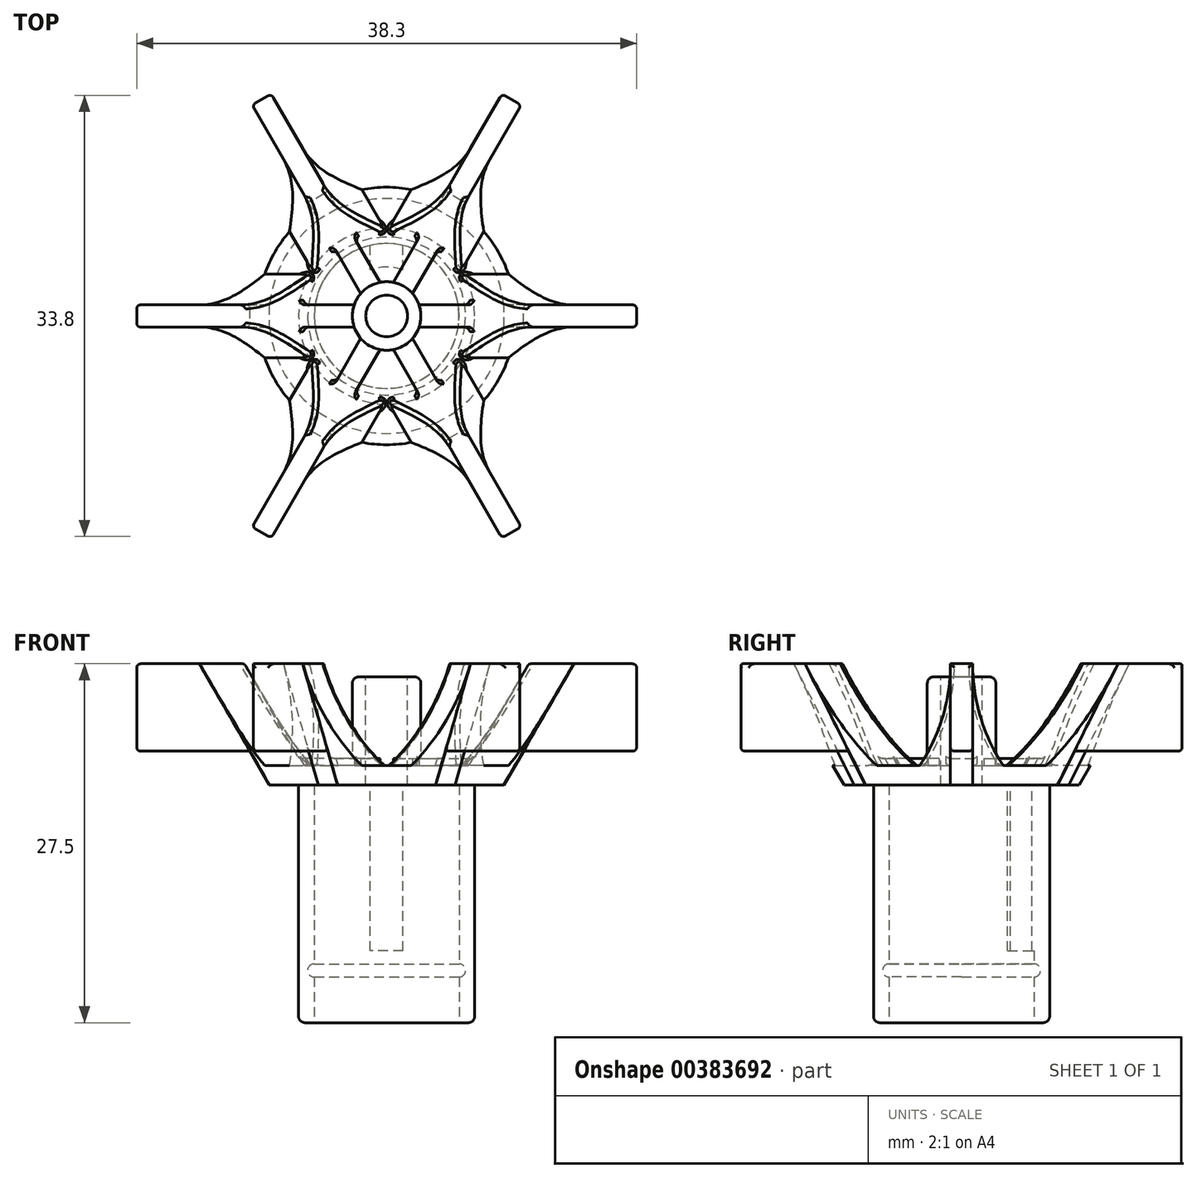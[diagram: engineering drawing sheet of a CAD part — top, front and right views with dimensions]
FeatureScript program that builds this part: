
annotation { "Feature Type Name" : "Feature", "Feature Type Description" : "" }
export const myFeature = defineFeature(function(context is Context, id is Id, definition is map)
    precondition{}
    {
        {
            var Q0;
            Q0=qCreatedBy(makeId("Top.planeOp"),FACE);
            cPlane(context, id + "F0", {"entities" : qUnion([Q0]), "cplaneType" : CPlaneType.OFFSET, "offset" : 26.5 * mm, "width" : 152.4 * mm, "height" : 152.4 * mm});
        }
        {
            var Q0;
            Q0=qCreatedBy(makeId("Front.planeOp"),FACE);
            var sketch = newSketch(context, id + "F1", { "sketchPlane" : qUnion([Q0])});
            skLineSegment(sketch, "E0", {"start": v(0, 29.25) * mm, "end": v(0, 3.34) * mm, "construction": true});
            skSolve(sketch);
        }
        {
            var Q0;
            Q0=qCreatedBy(makeId("Top.planeOp"),FACE);
            var sketch = newSketch(context, id + "F2", { "sketchPlane" : qUnion([Q0])});
            skCircle(sketch, "E1", {"center": v(0, 0) * mm, "radius": 6.75 * mm});
            skSolve(sketch);
        }
        {
            var Q0;
            Q0=makeQuery(id+"F2.imprint","IMPRINT",FACE,{"disambiguationData":[TD([[makeQuery(id+"F2.imprint","IMPRINT",EDGE,{"derivedFrom":sQuery(id+"F2.wireOp",EDGE,"E1")}),1.0]])]});
            extrude(context, id + "F3", {"entities" : qUnion([Q0]), "depth" : 19.7 * mm});
        }
        {
            var Q0;
            Q0=makeQuery(id+"F3.opExtrude","CAP_FACE",FACE,{"disambiguationData":[OSD([sQuery(id+"F2.wireOp",EDGE,"E1")])],"isStart":false});
            var sketch = newSketch(context, id + "F4", { "sketchPlane" : qUnion([Q0])});
            skCircle(sketch, "E2", {"center": v(0, 0) * mm, "radius": 8.38 * mm});
            skSolve(sketch);
        }
        {
            var Q0;
            Q0 = qSketchRegion(id + "F4", true);
            extrude(context, id + "F5", {"entities" : qUnion([Q0]), "operationType" : NewBodyOperationType.ADD, "oppositeDirection" : true, "depth" : 1.5 * mm});
        }
        {
            var Q0;
            Q0=makeQuery(id+"F3.opExtrude","CAP_FACE",FACE,{"disambiguationData":[OSD([sQuery(id+"F2.wireOp",EDGE,"E1")])],"isStart":true});
            var sketch = newSketch(context, id + "F6", { "sketchPlane" : qUnion([Q0])});
            skCircle(sketch, "E3", {"center": v(0, 0) * mm, "radius": 5.55 * mm});
            skSolve(sketch);
        }
        {
            var Q0;
            Q0=makeQuery(id+"F6.imprint","IMPRINT",FACE,{"disambiguationData":[TD([[makeQuery(id+"F6.imprint","IMPRINT",EDGE,{"derivedFrom":sQuery(id+"F6.wireOp",EDGE,"E3")}),1.0]])]});
            var Q1;
            Q1=makeQuery(id+"F5.opExtrude","CAP_FACE",FACE,{"disambiguationData":[OSD([sQuery(id+"F4.wireOp",EDGE,"E2")])],"isStart":false});
            extrude(context, id + "F7", {"entities" : qUnion([Q0]), "operationType" : NewBodyOperationType.REMOVE, "endBound" : BoundingType.UP_TO_SURFACE, "oppositeDirection" : true, "endBoundEntityFace" : qUnion([Q1]), "depth" : 25.4 * mm});
        }
        {
            var Q0;
            Q0=makeQuery(id+"F5.boolean.opBoolean","MERGE",FACE,{"derivedFrom":[makeQuery(id+"F3.opExtrude","CAP_FACE",FACE,{"disambiguationData":[OSD([sQuery(id+"F2.wireOp",EDGE,"E1")])],"isStart":false}),makeQuery(id+"F5.opExtrude","CAP_FACE",FACE,{"disambiguationData":[OSD([sQuery(id+"F4.wireOp",EDGE,"E2")])],"isStart":true})]});
            var sketch = newSketch(context, id + "F8", { "sketchPlane" : qUnion([Q0])});
            skCircle(sketch, "E4", {"center": v(0, 0) * mm, "radius": 2.62 * mm});
            skSolve(sketch);
        }
        {
            var Q0;
            Q0 = qSketchRegion(id + "F8", true);
            var Q1;
            Q1=qCreatedBy(id+"F0.planeOp",FACE);
            extrude(context, id + "F9", {"entities" : qUnion([Q0]), "operationType" : NewBodyOperationType.ADD, "endBound" : BoundingType.UP_TO_SURFACE, "endBoundEntityFace" : qUnion([Q1]), "depth" : 25.4 * mm});
        }
        {
            var Q0;
            Q0=makeQuery(id+"F9.opExtrude","CAP_FACE",FACE,{"disambiguationData":[OSD([sQuery(id+"F8.wireOp",EDGE,"E4")])],"isStart":false});
            var sketch = newSketch(context, id + "F10", { "sketchPlane" : qUnion([Q0])});
            skCircle(sketch, "E5", {"center": v(0, 0) * mm, "radius": 1.6 * mm});
            skSolve(sketch);
        }
        {
            var Q0;
            Q0 = qSketchRegion(id + "F10", true);
            extrude(context, id + "F11", {"entities" : qUnion([Q0]), "operationType" : NewBodyOperationType.REMOVE, "endBound" : BoundingType.THROUGH_ALL, "oppositeDirection" : true, "depth" : 25.4 * mm});
        }
        {
            var Q0;
            Q0=qCreatedBy(makeId("Front.planeOp"),FACE);
            var sketch = newSketch(context, id + "F12", { "sketchPlane" : qUnion([Q0])});
            skLineSegment(sketch, "E6", {"start": v(1.6, 19.7) * mm, "end": v(1.6, 20.25) * mm});
            skLineSegment(sketch, "E7", {"start": v(1.6, 20.25) * mm, "end": v(6.72, 20.25) * mm});
            skLineSegment(sketch, "E8", {"start": v(6.72, 20.25) * mm, "end": v(10.9, 27.5) * mm});
            skLineSegment(sketch, "E9", {"start": v(10.9, 27.5) * mm, "end": v(19.15, 27.5) * mm});
            skLineSegment(sketch, "E10", {"start": v(19.15, 27.5) * mm, "end": v(19.15, 20.8) * mm});
            skLineSegment(sketch, "E11", {"start": v(19.15, 20.8) * mm, "end": v(10.5, 20.8) * mm});
            skLineSegment(sketch, "E12", {"start": v(10.5, 20.8) * mm, "end": v(9, 18.2) * mm});
            skLineSegment(sketch, "E13", {"start": v(9, 18.2) * mm, "end": v(6.75, 18.2) * mm});
            skLineSegment(sketch, "E14", {"start": v(6.75, 18.2) * mm, "end": v(6.75, 19.7) * mm});
            skLineSegment(sketch, "E15", {"start": v(6.75, 19.7) * mm, "end": v(1.6, 19.7) * mm});
            skLineSegment(sketch, "E16", {"start": v(1.6, 20.25) * mm, "end": v(1.6, 26.5) * mm, "construction": true});
            skSolve(sketch);
        }
        {
            var Q0;
            Q0 = qSketchRegion(id + "F12", true);
            extrude(context, id + "F13", {"entities" : qUnion([Q0]), "operationType" : NewBodyOperationType.ADD, "endBound" : BoundingType.SYMMETRIC, "depth" : 1.7 * mm});
        }
        {
            var Q0;
            Q0=makeQuery(id+"F9.opExtrude","CAP_EDGE",EDGE,{"disambiguationData":[OSD([sQuery(id+"F8.wireOp",EDGE,"E4")])],"isStart":false});
            var Q1;
            Q1=makeQuery(id+"FnX98SisdUr0QIh_1.opPattern","COPY",EDGE,{"derivedFrom":makeQuery(id+"F5.opExtrude","CAP_EDGE",EDGE,{"disambiguationData":[OSD([sQuery(id+"F4.wireOp",EDGE,"E2")])],"isStart":true}),"instanceName":"2"});
            var Q2;
            Q2=makeQuery(id+"F7.boolean.opBoolean","COPY",EDGE,{"derivedFrom":makeQuery(id+"F7.opExtrude","CAP_EDGE",EDGE,{"disambiguationData":[OSD([sQuery(id+"F6.wireOp",EDGE,"E3")])],"isStart":true})});
            var Q3;
            Q3=makeQuery(id+"F3.opExtrude","CAP_EDGE",EDGE,{"disambiguationData":[OSD([sQuery(id+"F2.wireOp",EDGE,"E1")])],"isStart":true});
            var Q4;
            Q4=makeQuery(id+"F5.opExtrude","CAP_EDGE",EDGE,{"disambiguationData":[OSD([sQuery(id+"F4.wireOp",EDGE,"E2")])],"isStart":true});
            var Q5;
            Q5=makeQuery(id+"F9.opExtrude","CAP_EDGE",EDGE,{"disambiguationData":[OSD([sQuery(id+"F8.wireOp",EDGE,"E4")])],"isStart":true});
            fillet(context, id + "F14", {"entities" : qUnion([Q0, Q1, Q2, Q3, Q4, Q5]), "radius" : .5 * mm, "tangentPropagation" : true, "allowEdgeOverflow" : false});
        }
        {
            var Q0;
            Q0=qCreatedBy(makeId("Front.planeOp"),FACE);
            var sketch = newSketch(context, id + "F15", { "sketchPlane" : qUnion([Q0])});
            skLineSegment(sketch, "E17", {"start": v(14.37, 27.5) * mm, "end": v(10.9, 27.5) * mm});
            skLineSegment(sketch, "E18", {"start": v(10.9, 27.5) * mm, "end": v(5.54, 18.2) * mm});
            skLineSegment(sketch, "E19", {"start": v(5.54, 18.2) * mm, "end": v(9, 18.2) * mm});
            skLineSegment(sketch, "E20", {"start": v(9, 18.2) * mm, "end": v(14.37, 27.5) * mm});
            skSolve(sketch);
        }
        {
            var Q0;
            Q0 = qSketchRegion(id + "F15", true);
            var Q1;
            Q1=sQuery(id+"F1.wireOp",EDGE,"E0");
            revolve(context, id + "F16", {"operationType" : NewBodyOperationType.ADD, "entities" : qUnion([Q0]), "axis" : qUnion([Q1]), "revolveType" : RevolveType.SYMMETRIC, "angle" : 60 * degree});
        }
        {
            var Q0;
            Q0=qCreatedBy(makeId("Right.planeOp"),FACE);
            cPlane(context, id + "F17", {"entities" : qUnion([Q0]), "cplaneType" : CPlaneType.OFFSET, "offset" : 4.65 * mm, "width" : 152.4 * mm, "height" : 152.4 * mm});
        }
        {
            var Q0;
            Q0=qCreatedBy(id+"F17.planeOp",FACE);
            var sketch = newSketch(context, id + "F18", { "sketchPlane" : qUnion([Q0])});
            skPoint(sketch, "E21", {"position": v(4.93, 19.7) * mm});
            skLineSegment(sketch, "E22", {"start": v(0.85, 27.5) * mm, "end": v(7.18, 27.5) * mm});
            skLineSegment(sketch, "E23", {"start": v(7.18, 27.5) * mm, "end": v(4.93, 19.7) * mm});
            skLineSegment(sketch, "E24.MirrorCS", {"start": v(-0.85, 27.5) * mm, "end": v(-7.18, 27.5) * mm});
            skLineSegment(sketch, "E25.MirrorCS", {"start": v(-7.18, 27.5) * mm, "end": v(-4.93, 19.7) * mm});
            skPoint(sketch, "E26.MirrorCS.end.orphan", {"position": v(-4.93, 19.7) * mm});
            skPoint(sketch, "E26.MirrorCS.start.orphan", {"position": v(-0.85, 27.5) * mm});
            skLineSegment(sketch, "E27", {"start": v(4.93, 19.7) * mm, "end": v(3.2, 19.7) * mm});
            skArc(sketch, "E28", {"start": v(0.85, 27.5) * mm, "mid": v(1.45, 23.43) * mm, "end": v(3.2, 19.7) * mm});
            skLineSegment(sketch, "E29", {"start": v(0.85, 27.5) * mm, "end": v(0.85, 19.7) * mm, "construction": true});
            skArc(sketch, "E30.MirrorCS", {"start": v(-0.85, 27.5) * mm, "mid": v(-1.45, 23.43) * mm, "end": v(-3.2, 19.7) * mm});
            skLineSegment(sketch, "E31.MirrorCS", {"start": v(-4.93, 19.7) * mm, "end": v(-3.2, 19.7) * mm});
            skSolve(sketch);
        }
        {
            var Q0;
            Q0 = qSketchRegion(id + "F18", true);
            var Q1;
            Q1=makeQuery(id+"F13.opExtrude","SWEPT_FACE",FACE,{"disambiguationData":[OSD([sQuery(id+"F12.wireOp",EDGE,"E10")])]});
            extrude(context, id + "F19", {"entities" : qUnion([Q0]), "operationType" : NewBodyOperationType.REMOVE, "endBound" : BoundingType.UP_TO_SURFACE, "endBoundEntityFace" : qUnion([Q1]), "depth" : 25.4 * mm});
        }
        {
            var Q0;
            Q0=makeQuery(id+"F19.boolean.opBoolean","INTERSECT",EDGE,{"derivedFrom":[makeQuery(id+"F16.opRevolve","SWEPT_FACE",FACE,{"disambiguationData":[OSD([sQuery(id+"F15.wireOp",EDGE,"E18")])]}),makeQuery(id+"F19.opExtrude","SWEPT_FACE",FACE,{"disambiguationData":[OSD([sQuery(id+"F18.wireOp",EDGE,"E28")])]})]});
            var Q1;
            Q1=makeQuery(id+"F16.opRevolve","SWEPT_EDGE",EDGE,{"disambiguationData":[OSD([sQuery(id+"F15.wireOp",EDGE,"E17"),sQuery(id+"F15.wireOp",EDGE,"E18")])]});
            var Q2;
            Q2=makeQuery(id+"F19.boolean.opBoolean","INTERSECT",EDGE,{"derivedFrom":[makeQuery(id+"F16.opRevolve","SWEPT_FACE",FACE,{"disambiguationData":[OSD([sQuery(id+"F15.wireOp",EDGE,"E18")])]}),makeQuery(id+"F19.opExtrude","SWEPT_FACE",FACE,{"disambiguationData":[OSD([sQuery(id+"F18.wireOp",EDGE,"E30.MirrorCS")])]})]});
            var Q3;
            Q3=makeQuery(id+"F16.boolean.opBoolean","INTERSECT",EDGE,{"disambiguationData":[OD(0.0)],"derivedFrom":[makeQuery(id+"F5.boolean.opBoolean","MERGE",FACE,{"derivedFrom":[makeQuery(id+"F3.opExtrude","CAP_FACE",FACE,{"disambiguationData":[OSD([sQuery(id+"F2.wireOp",EDGE,"E1")])],"isStart":false}),makeQuery(id+"F5.opExtrude","CAP_FACE",FACE,{"disambiguationData":[OSD([sQuery(id+"F4.wireOp",EDGE,"E2")])],"isStart":true})]}),makeQuery(id+"F16.opRevolve","SWEPT_FACE",FACE,{"disambiguationData":[OSD([sQuery(id+"F15.wireOp",EDGE,"E18")])]})]});
            var Q4;
            Q4=makeQuery(id+"F16.boolean.opBoolean","INTERSECT",EDGE,{"derivedFrom":[makeQuery(id+"F13.opExtrude","SWEPT_FACE",FACE,{"disambiguationData":[OSD([sQuery(id+"F12.wireOp",EDGE,"E7")])]}),makeQuery(id+"F16.opRevolve","SWEPT_FACE",FACE,{"disambiguationData":[OSD([sQuery(id+"F15.wireOp",EDGE,"E18")])]})]});
            var Q5;
            Q5=makeQuery(id+"F16.boolean.opBoolean","INTERSECT",EDGE,{"disambiguationData":[OD(1.0)],"derivedFrom":[makeQuery(id+"F5.boolean.opBoolean","MERGE",FACE,{"derivedFrom":[makeQuery(id+"F3.opExtrude","CAP_FACE",FACE,{"disambiguationData":[OSD([sQuery(id+"F2.wireOp",EDGE,"E1")])],"isStart":false}),makeQuery(id+"F5.opExtrude","CAP_FACE",FACE,{"disambiguationData":[OSD([sQuery(id+"F4.wireOp",EDGE,"E2")])],"isStart":true})]}),makeQuery(id+"F16.opRevolve","SWEPT_FACE",FACE,{"disambiguationData":[OSD([sQuery(id+"F15.wireOp",EDGE,"E18")])]})]});
            var Q6;
            Q6=makeQuery(id+"F16.boolean.opBoolean","INTERSECT",EDGE,{"derivedFrom":[makeQuery(id+"F13.opExtrude","CAP_FACE",FACE,{"disambiguationData":[OSD([sQuery(id+"F12.wireOp",EDGE,"E6"),sQuery(id+"F12.wireOp",EDGE,"E7"),sQuery(id+"F12.wireOp",EDGE,"E8"),sQuery(id+"F12.wireOp",EDGE,"E9"),sQuery(id+"F12.wireOp",EDGE,"E10"),sQuery(id+"F12.wireOp",EDGE,"E11"),sQuery(id+"F12.wireOp",EDGE,"E12"),sQuery(id+"F12.wireOp",EDGE,"E13"),sQuery(id+"F12.wireOp",EDGE,"E14"),sQuery(id+"F12.wireOp",EDGE,"E15")])],"isStart":true}),makeQuery(id+"F16.opRevolve","SWEPT_FACE",FACE,{"disambiguationData":[OSD([sQuery(id+"F15.wireOp",EDGE,"E18")])]})]});
            var Q7;
            Q7=makeQuery(id+"F16.boolean.opBoolean","INTERSECT",EDGE,{"derivedFrom":[makeQuery(id+"F13.opExtrude","CAP_FACE",FACE,{"disambiguationData":[OSD([sQuery(id+"F12.wireOp",EDGE,"E6"),sQuery(id+"F12.wireOp",EDGE,"E7"),sQuery(id+"F12.wireOp",EDGE,"E8"),sQuery(id+"F12.wireOp",EDGE,"E9"),sQuery(id+"F12.wireOp",EDGE,"E10"),sQuery(id+"F12.wireOp",EDGE,"E11"),sQuery(id+"F12.wireOp",EDGE,"E12"),sQuery(id+"F12.wireOp",EDGE,"E13"),sQuery(id+"F12.wireOp",EDGE,"E14"),sQuery(id+"F12.wireOp",EDGE,"E15")])],"isStart":false}),makeQuery(id+"F16.opRevolve","SWEPT_FACE",FACE,{"disambiguationData":[OSD([sQuery(id+"F15.wireOp",EDGE,"E18")])]})]});
            var Q8;
            Q8=makeQuery(id+"F19.boolean.opBoolean","COPY",EDGE,{"derivedFrom":makeQuery(id+"F19.opExtrude","SWEPT_EDGE",EDGE,{"disambiguationData":[OSD([sQuery(id+"F18.wireOp",EDGE,"E24.MirrorCS"),sQuery(id+"F18.wireOp",EDGE,"E30.MirrorCS")])]})});
            var Q9;
            Q9=makeQuery(id+"F19.boolean.opBoolean","COPY",EDGE,{"derivedFrom":makeQuery(id+"F19.opExtrude","SWEPT_EDGE",EDGE,{"disambiguationData":[OSD([sQuery(id+"F18.wireOp",EDGE,"E22"),sQuery(id+"F18.wireOp",EDGE,"E28")])]})});
            var Q10;
            Q10=makeQuery(id+"F13.opExtrude","SWEPT_EDGE",EDGE,{"disambiguationData":[OSD([sQuery(id+"F12.wireOp",EDGE,"E9"),sQuery(id+"F12.wireOp",EDGE,"E10")])]});
            var Q11;
            Q11=makeQuery(id+"F13.opExtrude","CAP_EDGE",EDGE,{"disambiguationData":[OSD([sQuery(id+"F12.wireOp",EDGE,"E10")])],"isStart":false});
            var Q12;
            Q12=makeQuery(id+"F13.opExtrude","CAP_EDGE",EDGE,{"disambiguationData":[OSD([sQuery(id+"F12.wireOp",EDGE,"E10")])],"isStart":true});
            var Q13;
            Q13=makeQuery(id+"F13.opExtrude","CAP_EDGE",EDGE,{"disambiguationData":[OSD([sQuery(id+"F12.wireOp",EDGE,"E11")])],"isStart":true});
            var Q14;
            Q14=makeQuery(id+"F13.opExtrude","SWEPT_EDGE",EDGE,{"disambiguationData":[OSD([sQuery(id+"F12.wireOp",EDGE,"E10"),sQuery(id+"F12.wireOp",EDGE,"E11")])]});
            var Q15;
            Q15=makeQuery(id+"F13.opExtrude","CAP_EDGE",EDGE,{"disambiguationData":[OSD([sQuery(id+"F12.wireOp",EDGE,"E11")])],"isStart":false});
            fillet(context, id + "F20", {"entities" : qUnion([Q0, Q1, Q2, Q3, Q4, Q5, Q6, Q7, Q8, Q9, Q10, Q11, Q12, Q13, Q14, Q15]), "radius" : .3 * mm, "tangentPropagation" : true, "allowEdgeOverflow" : false});
        }
        {
            var Q0;
            Q0=makeQuery(id+"F3.opExtrude","SWEPT_BODY",BODY,{"disambiguationData":[OSD([sQuery(id+"F2.wireOp",EDGE,"E1")])]});
            var Q1;
            Q1=sQuery(id+"F1.wireOp",EDGE,"E0");
            circularPattern(context, id + "F21", {"operationType" : NewBodyOperationType.ADD, "entities" : qUnion([Q0]), "axis" : qUnion([Q1]), "angle" : 360 * degree, "instanceCount" : 6, "equalSpace" : true});
        }
        {
            var Q0;
            Q0=makeQuery(id+"F3.opExtrude","SWEPT_BODY",BODY,{"disambiguationData":[OSD([sQuery(id+"F2.wireOp",EDGE,"E1")])]});
            var Q1;
            Q1=sQuery(id+"F1.wireOp",EDGE,"E0");
            circularPattern(context, id + "F22", {"operationType" : NewBodyOperationType.ADD, "entities" : qUnion([Q0]), "axis" : qUnion([Q1]), "angle" : 360 * degree, "instanceCount" : 6, "equalSpace" : true});
        }
        {
            var Q0;
            Q0=qCreatedBy(makeId("Front.planeOp"),FACE);
            var sketch = newSketch(context, id + "F23", { "sketchPlane" : qUnion([Q0])});
            skCircle(sketch, "E32", {"center": v(5.55, 4) * mm, "radius": 0.5 * mm});
            skLineSegment(sketch, "E33", {"start": v(5.55, 4) * mm, "end": v(5.55, 0.38) * mm, "construction": true});
            skSolve(sketch);
        }
        {
            var Q0;
            Q0=makeQuery(id+"F23.imprint","IMPRINT",FACE,{"disambiguationData":[TD([[makeQuery(id+"F23.imprint","IMPRINT",EDGE,{"derivedFrom":sQuery(id+"F23.wireOp",EDGE,"E32")}),1.0]])]});
            var Q1;
            Q1=sQuery(id+"F1.wireOp",EDGE,"E0");
            revolve(context, id + "F24", {"operationType" : NewBodyOperationType.REMOVE, "entities" : qUnion([Q0]), "axis" : qUnion([Q1]), "revolveType" : RevolveType.FULL, "oppositeDirection" : true});
        }
        {
            var Q0;
            Q0=makeQuery(id+"F7.boolean.opBoolean","COPY",FACE,{"derivedFrom":makeQuery(id+"F7.opExtrude","CAP_FACE",FACE,{"disambiguationData":[OSD([sQuery(id+"F6.wireOp",EDGE,"E3")])],"isStart":false})});
            var sketch = newSketch(context, id + "F25", { "sketchPlane" : qUnion([Q0])});
            skLineSegment(sketch, "E34.top", {"start": v(-1.25, -6.63) * mm, "end": v(1.25, -6.63) * mm});
            skLineSegment(sketch, "E34.left", {"start": v(-1.25, -3.54) * mm, "end": v(-1.25, -6.63) * mm});
            skLineSegment(sketch, "E34.right", {"start": v(1.25, -3.54) * mm, "end": v(1.25, -6.63) * mm});
            skLineSegment(sketch, "E35", {"start": v(0, 0) * mm, "end": v(0, -6.63) * mm, "construction": true});
            skArc(sketch, "E36", {"start": v(-1.25, -3.54) * mm, "mid": v(0, -3.75) * mm, "end": v(1.25, -3.54) * mm});
            skPoint(sketch, "E37.orphan", {"position": v(-1.25, 0) * mm});
            skPoint(sketch, "E34.bottom.end.orphan", {"position": v(1.25, 0) * mm});
            skSolve(sketch);
        }
        {
            var Q0;
            {var subQ0=sQuery(id+"F25.wireOp",EDGE,"E36");Q0=makeQuery(id+"F25.imprint","IMPRINT",FACE,{"disambiguationData":[TD([[makeQuery(id+"F25.imprint","IMPRINT",EDGE,{"derivedFrom":subQ0}),-1.0]])]});}
            extrude(context, id + "F26", {"entities" : qUnion([Q0]), "operationType" : NewBodyOperationType.ADD, "depth" : 12.7 * mm});
        }
    });
